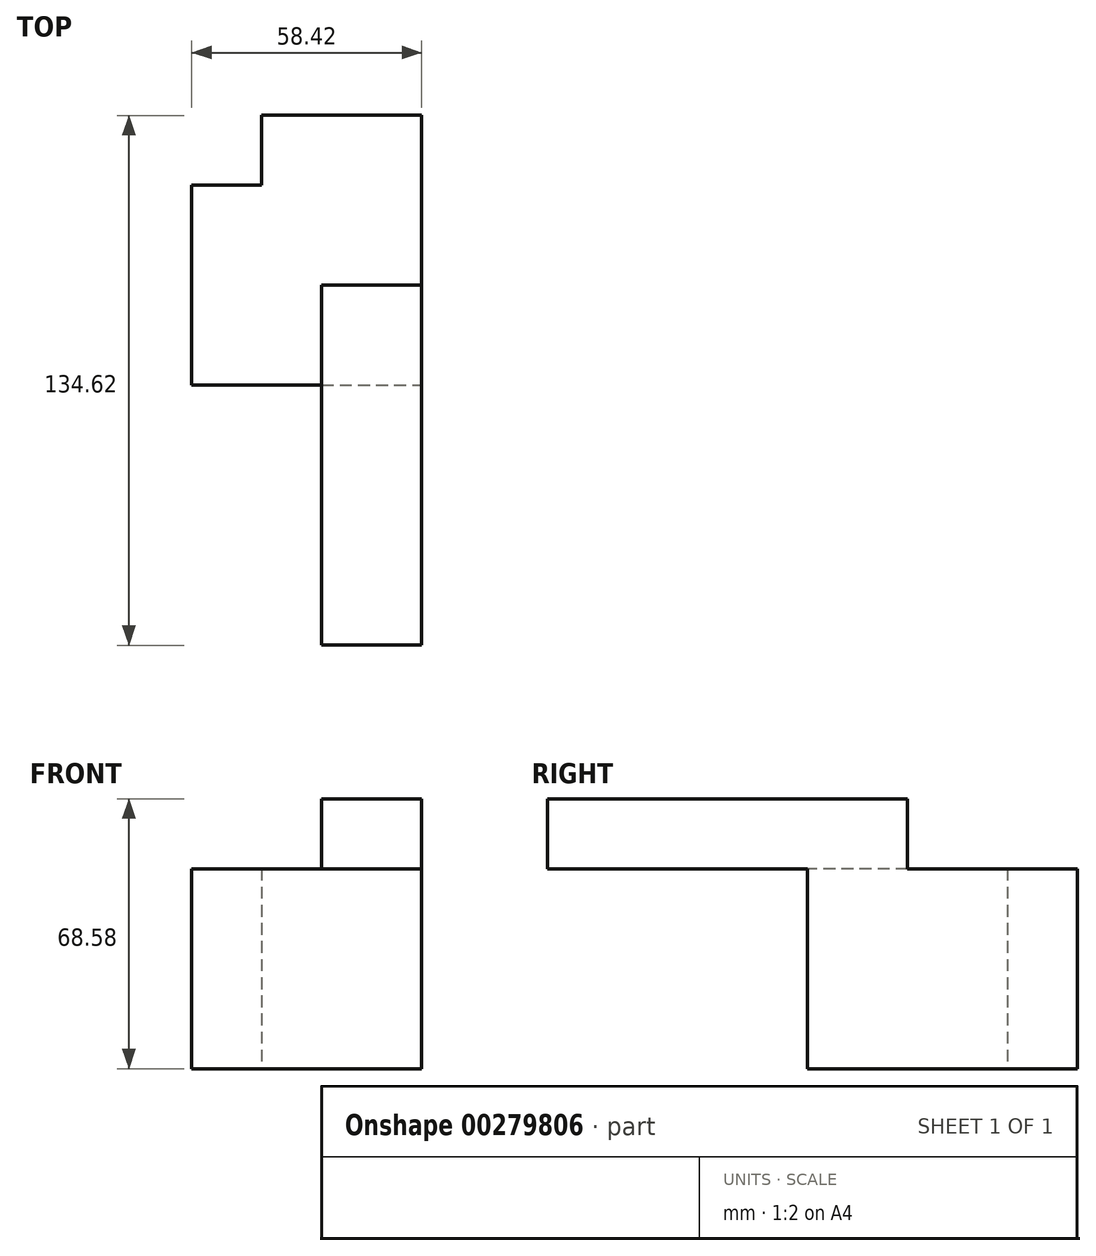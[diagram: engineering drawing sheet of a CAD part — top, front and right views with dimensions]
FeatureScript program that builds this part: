
annotation { "Feature Type Name" : "Feature", "Feature Type Description" : "" }
export const myFeature = defineFeature(function(context is Context, id is Id, definition is map)
    precondition{}
    {
        {
            var Q0;
            Q0=qCreatedBy(makeId("Right.planeOp"),FACE);
            var sketch = newSketch(context, id + "F0", { "sketchPlane" : qUnion([Q0])});
            skLineSegment(sketch, "E0.bottom", {"start": v(13.16, 33.1) * mm, "end": v(-78.28, 33.1) * mm});
            skLineSegment(sketch, "E0.top", {"start": v(13.16, 15.32) * mm, "end": v(-78.28, 15.32) * mm});
            skLineSegment(sketch, "E0.left", {"start": v(13.16, 33.1) * mm, "end": v(13.16, 15.32) * mm});
            skLineSegment(sketch, "E0.right", {"start": v(-78.28, 33.1) * mm, "end": v(-78.28, 15.32) * mm});
            skSolve(sketch);
        }
        {
            var Q0;
            Q0 = qSketchRegion(id + "F0", true);
            extrude(context, id + "F1", {"entities" : qUnion([Q0]), "depth" : 25.4 * mm});
        }
        {
            var Q0;
            Q0=makeQuery(id+"F1.opExtrude","SWEPT_FACE",FACE,{"disambiguationData":[OSD([sQuery(id+"F0.wireOp",EDGE,"E0.top")])]});
            var sketch = newSketch(context, id + "F2", { "sketchPlane" : qUnion([Q0])});
            skLineSegment(sketch, "E1", {"start": v(0, 12.24) * mm, "end": v(25.4, 12.24) * mm});
            skSolve(sketch);
        }
        {
            var Q0;
            {var subQ0=sQuery(id+"F2.wireOp",EDGE,"E1");Q0=makeQuery(id+"F2.imprint","IMPRINT",FACE,{"disambiguationData":[TD([[makeQuery(id+"F2.imprint","IMPRINT",EDGE,{"derivedFrom":subQ0}),-1.0]])]});}
            extrude(context, id + "F3", {"entities" : qUnion([Q0]), "operationType" : NewBodyOperationType.ADD, "depth" : 50.8 * mm});
        }
        {
            var Q0;
            {var subQ0=sQuery(id+"F0.wireOp",EDGE,"E0.left");Q0=makeQuery(id+"F3.boolean.opBoolean","MERGE",FACE,{"derivedFrom":[makeQuery(id+"F1.opExtrude","SWEPT_FACE",FACE,{"disambiguationData":[OSD([subQ0])]}),makeQuery(id+"F3.opExtrude","SWEPT_FACE",FACE,{"disambiguationData":[OSD([sQuery(id+"F0.wireOp",EDGE,"E0.top"),subQ0])]})]});}
            var sketch = newSketch(context, id + "F4", { "sketchPlane" : qUnion([Q0])});
            skLineSegment(sketch, "E2", {"start": v(-25.4, 15.32) * mm, "end": v(0, 15.32) * mm});
            skSolve(sketch);
        }
        {
            var Q0;
            {var subQ0=sQuery(id+"F4.wireOp",EDGE,"E2");Q0=makeQuery(id+"F4.imprint","IMPRINT",FACE,{"disambiguationData":[TD([[makeQuery(id+"F4.imprint","IMPRINT",EDGE,{"derivedFrom":subQ0}),-1.0]])]});}
            extrude(context, id + "F5", {"entities" : qUnion([Q0]), "operationType" : NewBodyOperationType.ADD, "depth" : 43.18 * mm});
        }
        {
            var Q0;
            {var subQ0=sQuery(id+"F0.wireOp",EDGE,"E0.top");var subQ1=makeQuery(id+"F1.opExtrude","CAP_EDGE",EDGE,{"disambiguationData":[OSD([subQ0])],"isStart":true});var subQ2=sQuery(id+"F0.wireOp",EDGE,"E0.left");var subQ3=makeQuery(id+"F2.imprint","INTERSECT",VERTEX,{"derivedFrom":[makeQuery(id+"F1.opExtrude","SWEPT_EDGE",EDGE,{"disambiguationData":[OSD([subQ0,subQ2])]}),subQ1]});var subQ4=makeQuery(id+"F3.boolean.opBoolean","MERGE",EDGE,{"derivedFrom":[makeQuery(id+"F1.opExtrude","CAP_EDGE",EDGE,{"disambiguationData":[OSD([subQ2])],"isStart":true}),makeQuery(id+"F3.opExtrude","SWEPT_EDGE",EDGE,{"disambiguationData":[OSD([subQ0,subQ2]),TDD([subQ3])]})]});Q0=makeQuery(id+"F5.boolean.opBoolean","MERGE",FACE,{"derivedFrom":[makeQuery(id+"F3.boolean.opBoolean","MERGE",FACE,{"derivedFrom":[makeQuery(id+"F1.opExtrude","CAP_FACE",FACE,{"disambiguationData":[OSD([sQuery(id+"F0.wireOp",EDGE,"E0.bottom"),subQ0,subQ2,sQuery(id+"F0.wireOp",EDGE,"E0.right")])],"isStart":true}),makeQuery(id+"F3.opExtrude","SWEPT_FACE",FACE,{"disambiguationData":[OSD([subQ0]),TDD([makeQuery(id+"F2.imprint","IMPRINT",EDGE,{"disambiguationData":[TD([[makeQuery(id+"F2.imprint","INTERSECT",VERTEX,{"derivedFrom":[subQ1,sQuery(id+"F2.wireOp",EDGE,"E1")]}),1.0]])],"derivedFrom":subQ1})])]})]}),makeQuery(id+"F5.opExtrude","SWEPT_FACE",FACE,{"disambiguationData":[OSD([subQ0,subQ2]),TDD([makeQuery(id+"F4.imprint","IMPRINT",EDGE,{"disambiguationData":[TD([[makeQuery(id+"F4.imprint","INTERSECT",VERTEX,{"derivedFrom":[subQ4,sQuery(id+"F4.wireOp",EDGE,"E2")]}),-1.0]])],"derivedFrom":subQ4})])]})]});}
            var sketch = newSketch(context, id + "F6", { "sketchPlane" : qUnion([Q0])});
            skLineSegment(sketch, "E3", {"start": v(-13.16, 15.32) * mm, "end": v(12.24, 15.32) * mm});
            skSolve(sketch);
        }
        {
            var Q0;
            Q0=makeQuery(id+"F6.imprint","IMPRINT",FACE,{"disambiguationData":[TD([[makeQuery(id+"F6.imprint","IMPRINT",EDGE,{"derivedFrom":sQuery(id+"F6.wireOp",EDGE,"E3")}),-1.0]])]});
            extrude(context, id + "F7", {"entities" : qUnion([Q0]), "operationType" : NewBodyOperationType.ADD, "depth" : 15.24 * mm});
        }
        {
            var Q0;
            Q0=makeQuery(id+"F7.opExtrude","CAP_FACE",FACE,{"disambiguationData":[OSD([sQuery(id+"F0.wireOp",EDGE,"E0.top"),sQuery(id+"F0.wireOp",EDGE,"E0.left"),sQuery(id+"F2.wireOp",EDGE,"E1"),sQuery(id+"F4.wireOp",EDGE,"E2"),sQuery(id+"F6.wireOp",EDGE,"E3")])],"isStart":false});
            var sketch = newSketch(context, id + "F8", { "sketchPlane" : qUnion([Q0])});
            skLineSegment(sketch, "E4", {"start": v(-38.56, 15.32) * mm, "end": v(-38.56, -35.48) * mm});
            skSolve(sketch);
        }
        {
            var Q0;
            {var subQ0=sQuery(id+"F8.wireOp",EDGE,"E4");Q0=makeQuery(id+"F8.imprint","IMPRINT",FACE,{"disambiguationData":[TD([[makeQuery(id+"F8.imprint","IMPRINT",EDGE,{"derivedFrom":subQ0}),1.0]])]});}
            extrude(context, id + "F9", {"entities" : qUnion([Q0]), "operationType" : NewBodyOperationType.ADD, "depth" : 17.78 * mm});
        }
    });
